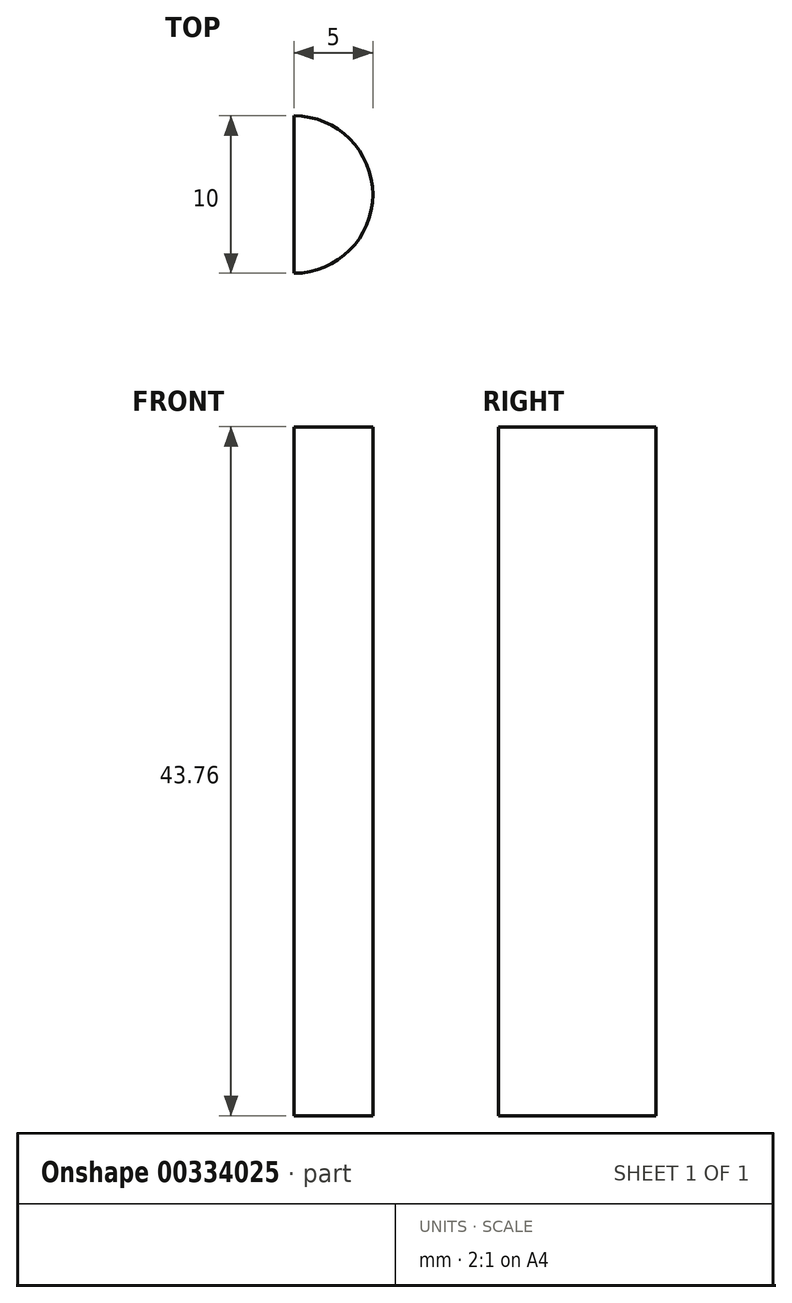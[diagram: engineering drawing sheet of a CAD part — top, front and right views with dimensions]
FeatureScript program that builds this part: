
annotation { "Feature Type Name" : "Feature", "Feature Type Description" : "" }
export const myFeature = defineFeature(function(context is Context, id is Id, definition is map)
    precondition{}
    {
        {
            var Q0;
            Q0=qCreatedBy(makeId("Front.planeOp"),FACE);
            var sketch = newSketch(context, id + "F0", { "sketchPlane" : qUnion([Q0])});
            skLineSegment(sketch, "E0.bottom", {"start": v(-17.17, 21.88) * mm, "end": v(-11.17, 21.88) * mm});
            skLineSegment(sketch, "E0.top", {"start": v(-17.17, 0) * mm, "end": v(-11.17, 0) * mm});
            skLineSegment(sketch, "E0.left", {"start": v(-17.17, 21.88) * mm, "end": v(-17.17, 0) * mm});
            skLineSegment(sketch, "E0.right", {"start": v(-11.17, 21.88) * mm, "end": v(-11.17, 0) * mm});
            skLineSegment(sketch, "E1", {"start": v(-38.95, 0) * mm, "end": v(39.14, 0) * mm, "construction": true});
            skLineSegment(sketch, "E2.bottom", {"start": v(-11.17, 21.88) * mm, "end": v(1.83, 21.88) * mm});
            skLineSegment(sketch, "E2.top", {"start": v(-11.17, 18) * mm, "end": v(1.83, 18) * mm});
            skLineSegment(sketch, "E2.left", {"start": v(-11.17, 21.88) * mm, "end": v(-11.17, 18) * mm});
            skLineSegment(sketch, "E2.right", {"start": v(1.83, 21.88) * mm, "end": v(1.83, 18) * mm});
            skLineSegment(sketch, "E3.bottom", {"start": v(1.83, 21.88) * mm, "end": v(3.33, 21.88) * mm});
            skLineSegment(sketch, "E3.top", {"start": v(1.83, 16.5) * mm, "end": v(3.33, 16.5) * mm});
            skLineSegment(sketch, "E3.left", {"start": v(1.83, 21.88) * mm, "end": v(1.83, 16.5) * mm});
            skLineSegment(sketch, "E3.right", {"start": v(3.33, 21.88) * mm, "end": v(3.33, 16.5) * mm});
            skLineSegment(sketch, "E4.MirrorCS", {"start": v(1.83, -16.5) * mm, "end": v(3.33, -16.5) * mm});
            skLineSegment(sketch, "E5.MirrorCS", {"start": v(1.83, -21.88) * mm, "end": v(3.33, -21.88) * mm});
            skLineSegment(sketch, "E6.MirrorCS", {"start": v(1.83, -21.88) * mm, "end": v(1.83, -18) * mm});
            skLineSegment(sketch, "E7.MirrorCS", {"start": v(-11.17, -21.88) * mm, "end": v(-11.17, -18) * mm});
            skLineSegment(sketch, "E8.MirrorCS", {"start": v(1.83, -21.88) * mm, "end": v(1.83, -16.5) * mm});
            skLineSegment(sketch, "E9.MirrorCS", {"start": v(-11.17, -18) * mm, "end": v(1.83, -18) * mm});
            skLineSegment(sketch, "E10.MirrorCS", {"start": v(3.33, -21.88) * mm, "end": v(3.33, -16.5) * mm});
            skLineSegment(sketch, "E11.MirrorCS", {"start": v(-11.17, -21.88) * mm, "end": v(1.83, -21.88) * mm});
            skLineSegment(sketch, "E12.MirrorCS", {"start": v(-11.17, -21.88) * mm, "end": v(-11.17, 0) * mm});
            skLineSegment(sketch, "E13.MirrorCS", {"start": v(-17.17, -21.88) * mm, "end": v(-11.17, -21.88) * mm});
            skLineSegment(sketch, "E14.MirrorCS", {"start": v(-17.17, -21.88) * mm, "end": v(-17.17, 0) * mm});
            skSolve(sketch);
        }
        {
            var Q0;
            Q0 = qSketchRegion(id + "F0", true);
            extrude(context, id + "F1", {"entities" : qUnion([Q0]), "depth" : 16 * mm});
        }
        {
            var Q0;
            Q0=makeQuery(id+"F1.opExtrude","SWEPT_FACE",FACE,{"disambiguationData":[OSD([sQuery(id+"F0.wireOp",EDGE,"E0.bottom"),sQuery(id+"F0.wireOp",EDGE,"E2.bottom"),sQuery(id+"F0.wireOp",EDGE,"E3.bottom")])]});
            var sketch = newSketch(context, id + "F2", { "sketchPlane" : qUnion([Q0])});
            skArc(sketch, "E15", {"start": v(-17.17, -3) * mm, "mid": v(-12.17, -8) * mm, "end": v(-17.17, -13) * mm});
            skSolve(sketch);
        }
        {
            var Q0;
            {var subQ0=sQuery(id+"F2.wireOp",EDGE,"E15");Q0=makeQuery(id+"F2.imprint","IMPRINT",FACE,{"disambiguationData":[TD([[makeQuery(id+"F2.imprint","IMPRINT",EDGE,{"derivedFrom":subQ0}),-1.0]])]});}
            extrude(context, id + "F3", {"entities" : qUnion([Q0]), "operationType" : NewBodyOperationType.REMOVE, "oppositeDirection" : true, "depth" : 100 * mm});
        }
    });
